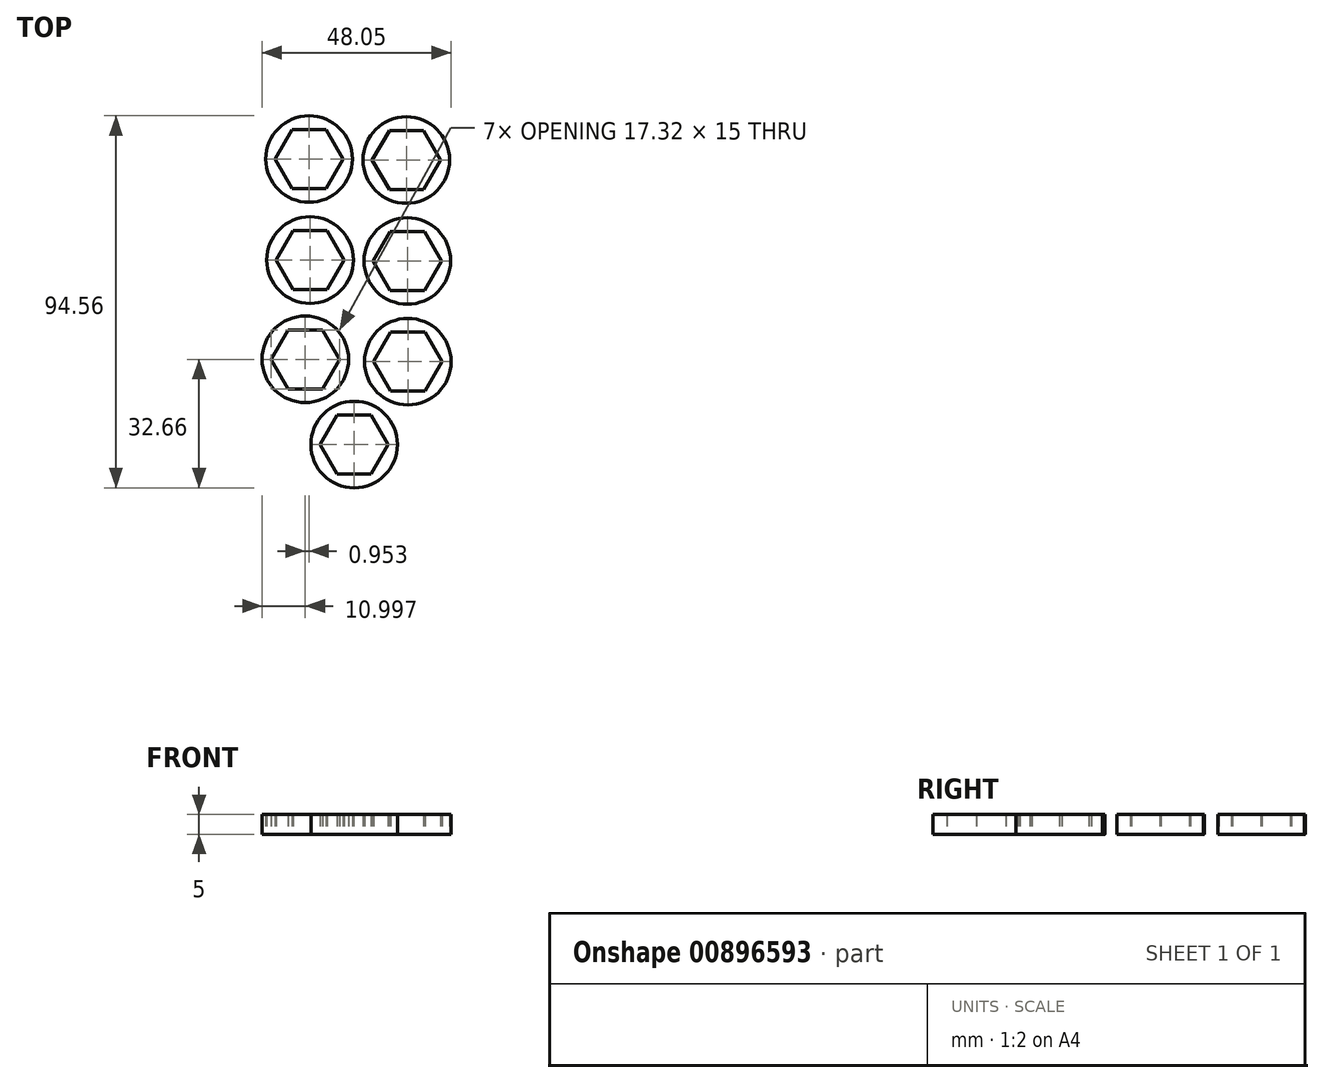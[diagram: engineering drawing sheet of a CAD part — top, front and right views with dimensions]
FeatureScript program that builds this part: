
annotation { "Feature Type Name" : "Feature", "Feature Type Description" : "" }
export const myFeature = defineFeature(function(context is Context, id is Id, definition is map)
    precondition{}
    {
        {
            var Q0;
            Q0=qCreatedBy(makeId("Top.planeOp"),FACE);
            var sketch = newSketch(context, id + "F0", { "sketchPlane" : qUnion([Q0])});
            skCircle(sketch, "E0.cCircle", {"center": v(0, 0) * mm, "radius": 7.5 * mm, "construction": true});
            skLineSegment(sketch, "E0.0", {"start": v(-4.33, 7.5) * mm, "end": v(4.33, 7.5) * mm});
            skLineSegment(sketch, "E0.1", {"start": v(4.33, 7.5) * mm, "end": v(8.66, 0) * mm});
            skLineSegment(sketch, "E0.2", {"start": v(8.66, 0) * mm, "end": v(4.33, -7.5) * mm});
            skLineSegment(sketch, "E0.3", {"start": v(4.33, -7.5) * mm, "end": v(-4.33, -7.5) * mm});
            skLineSegment(sketch, "E0.4", {"start": v(-4.33, -7.5) * mm, "end": v(-8.66, 0) * mm});
            skLineSegment(sketch, "E0.5", {"start": v(-8.66, 0) * mm, "end": v(-4.33, 7.5) * mm});
            skPoint(sketch, "E0.0.midPoint", {"position": v(0, 7.5) * mm});
            skCircle(sketch, "E1", {"center": v(0, 0) * mm, "radius": 11 * mm});
            skCircle(sketch, "E2.cCircle", {"center": v(-0.25, 25.64) * mm, "radius": 7.5 * mm, "construction": true});
            skLineSegment(sketch, "E2.0", {"start": v(-4.58, 33.14) * mm, "end": v(4.08, 33.14) * mm});
            skLineSegment(sketch, "E2.1", {"start": v(4.08, 33.14) * mm, "end": v(8.41, 25.64) * mm});
            skLineSegment(sketch, "E2.2", {"start": v(8.41, 25.64) * mm, "end": v(4.08, 18.14) * mm});
            skLineSegment(sketch, "E2.3", {"start": v(4.08, 18.14) * mm, "end": v(-4.58, 18.14) * mm});
            skLineSegment(sketch, "E2.4", {"start": v(-4.58, 18.14) * mm, "end": v(-8.9, 25.64) * mm});
            skLineSegment(sketch, "E2.5", {"start": v(-8.9, 25.64) * mm, "end": v(-4.58, 33.14) * mm});
            skPoint(sketch, "E2.0.midPoint", {"position": v(-0.25, 33.14) * mm});
            skCircle(sketch, "E3", {"center": v(-0.25, 25.64) * mm, "radius": 11 * mm});
            skCircle(sketch, "E4.cCircle", {"center": v(0.13, -25.6) * mm, "radius": 7.5 * mm, "construction": true});
            skLineSegment(sketch, "E4.0", {"start": v(-4.2, -18.1) * mm, "end": v(4.46, -18.1) * mm});
            skLineSegment(sketch, "E4.1", {"start": v(4.46, -18.1) * mm, "end": v(8.8, -25.6) * mm});
            skLineSegment(sketch, "E4.2", {"start": v(8.8, -25.6) * mm, "end": v(4.46, -33.1) * mm});
            skLineSegment(sketch, "E4.3", {"start": v(4.46, -33.1) * mm, "end": v(-4.2, -33.1) * mm});
            skLineSegment(sketch, "E4.4", {"start": v(-4.2, -33.1) * mm, "end": v(-8.53, -25.6) * mm});
            skLineSegment(sketch, "E4.5", {"start": v(-8.53, -25.6) * mm, "end": v(-4.2, -18.1) * mm});
            skPoint(sketch, "E4.0.midPoint", {"position": v(0.13, -18.1) * mm});
            skCircle(sketch, "E5", {"center": v(0.13, -25.6) * mm, "radius": 11 * mm});
            skCircle(sketch, "E6.cCircle", {"center": v(-24.97, 25.9) * mm, "radius": 7.5 * mm, "construction": true});
            skLineSegment(sketch, "E6.0", {"start": v(-29.3, 33.4) * mm, "end": v(-20.64, 33.4) * mm});
            skLineSegment(sketch, "E6.1", {"start": v(-20.64, 33.4) * mm, "end": v(-16.3, 25.9) * mm});
            skLineSegment(sketch, "E6.2", {"start": v(-16.3, 25.9) * mm, "end": v(-20.64, 18.4) * mm});
            skLineSegment(sketch, "E6.3", {"start": v(-20.64, 18.4) * mm, "end": v(-29.3, 18.4) * mm});
            skLineSegment(sketch, "E6.4", {"start": v(-29.3, 18.4) * mm, "end": v(-33.63, 25.9) * mm});
            skLineSegment(sketch, "E6.5", {"start": v(-33.63, 25.9) * mm, "end": v(-29.3, 33.4) * mm});
            skPoint(sketch, "E6.0.midPoint", {"position": v(-24.97, 33.4) * mm});
            skCircle(sketch, "E7", {"center": v(-24.97, 25.9) * mm, "radius": 11 * mm});
            skCircle(sketch, "E8.cCircle", {"center": v(-24.73, 0.22) * mm, "radius": 7.5 * mm, "construction": true});
            skLineSegment(sketch, "E8.0", {"start": v(-29.06, 7.72) * mm, "end": v(-20.4, 7.72) * mm});
            skLineSegment(sketch, "E8.1", {"start": v(-20.4, 7.72) * mm, "end": v(-16.07, 0.22) * mm});
            skLineSegment(sketch, "E8.2", {"start": v(-16.07, 0.22) * mm, "end": v(-20.4, -7.28) * mm});
            skLineSegment(sketch, "E8.3", {"start": v(-20.4, -7.28) * mm, "end": v(-29.06, -7.28) * mm});
            skLineSegment(sketch, "E8.4", {"start": v(-29.06, -7.28) * mm, "end": v(-33.39, 0.22) * mm});
            skLineSegment(sketch, "E8.5", {"start": v(-33.39, 0.22) * mm, "end": v(-29.06, 7.72) * mm});
            skPoint(sketch, "E8.0.midPoint", {"position": v(-24.73, 7.72) * mm});
            skCircle(sketch, "E9", {"center": v(-24.73, 0.22) * mm, "radius": 11 * mm});
            skCircle(sketch, "E10.cCircle", {"center": v(-25.92, -25) * mm, "radius": 7.5 * mm, "construction": true});
            skLineSegment(sketch, "E10.0", {"start": v(-30.25, -17.5) * mm, "end": v(-21.6, -17.5) * mm});
            skLineSegment(sketch, "E10.1", {"start": v(-21.6, -17.5) * mm, "end": v(-17.26, -25) * mm});
            skLineSegment(sketch, "E10.2", {"start": v(-17.26, -25) * mm, "end": v(-21.6, -32.5) * mm});
            skLineSegment(sketch, "E10.3", {"start": v(-21.6, -32.5) * mm, "end": v(-30.25, -32.5) * mm});
            skLineSegment(sketch, "E10.4", {"start": v(-30.25, -32.5) * mm, "end": v(-34.58, -25) * mm});
            skLineSegment(sketch, "E10.5", {"start": v(-34.58, -25) * mm, "end": v(-30.25, -17.5) * mm});
            skPoint(sketch, "E10.0.midPoint", {"position": v(-25.92, -17.5) * mm});
            skCircle(sketch, "E11", {"center": v(-25.92, -25) * mm, "radius": 11 * mm});
            skCircle(sketch, "E12.cCircle", {"center": v(-13.5, -46.66) * mm, "radius": 7.5 * mm, "construction": true});
            skLineSegment(sketch, "E12.0", {"start": v(-17.84, -39.16) * mm, "end": v(-9.18, -39.16) * mm});
            skLineSegment(sketch, "E12.1", {"start": v(-9.18, -39.16) * mm, "end": v(-4.85, -46.66) * mm});
            skLineSegment(sketch, "E12.2", {"start": v(-4.85, -46.66) * mm, "end": v(-9.18, -54.16) * mm});
            skLineSegment(sketch, "E12.3", {"start": v(-9.18, -54.16) * mm, "end": v(-17.84, -54.16) * mm});
            skLineSegment(sketch, "E12.4", {"start": v(-17.84, -54.16) * mm, "end": v(-22.17, -46.66) * mm});
            skLineSegment(sketch, "E12.5", {"start": v(-22.17, -46.66) * mm, "end": v(-17.84, -39.16) * mm});
            skPoint(sketch, "E12.0.midPoint", {"position": v(-13.5, -39.16) * mm});
            skCircle(sketch, "E13", {"center": v(-13.5, -46.66) * mm, "radius": 11 * mm});
            skSolve(sketch);
        }
        {
            var Q0;
            Q0 = qSketchRegion(id + "F0", true);
            extrude(context, id + "F1", {"entities" : qUnion([Q0]), "depth" : 5 * mm, "offsetDistance" : 25.4 * mm});
        }
    });
